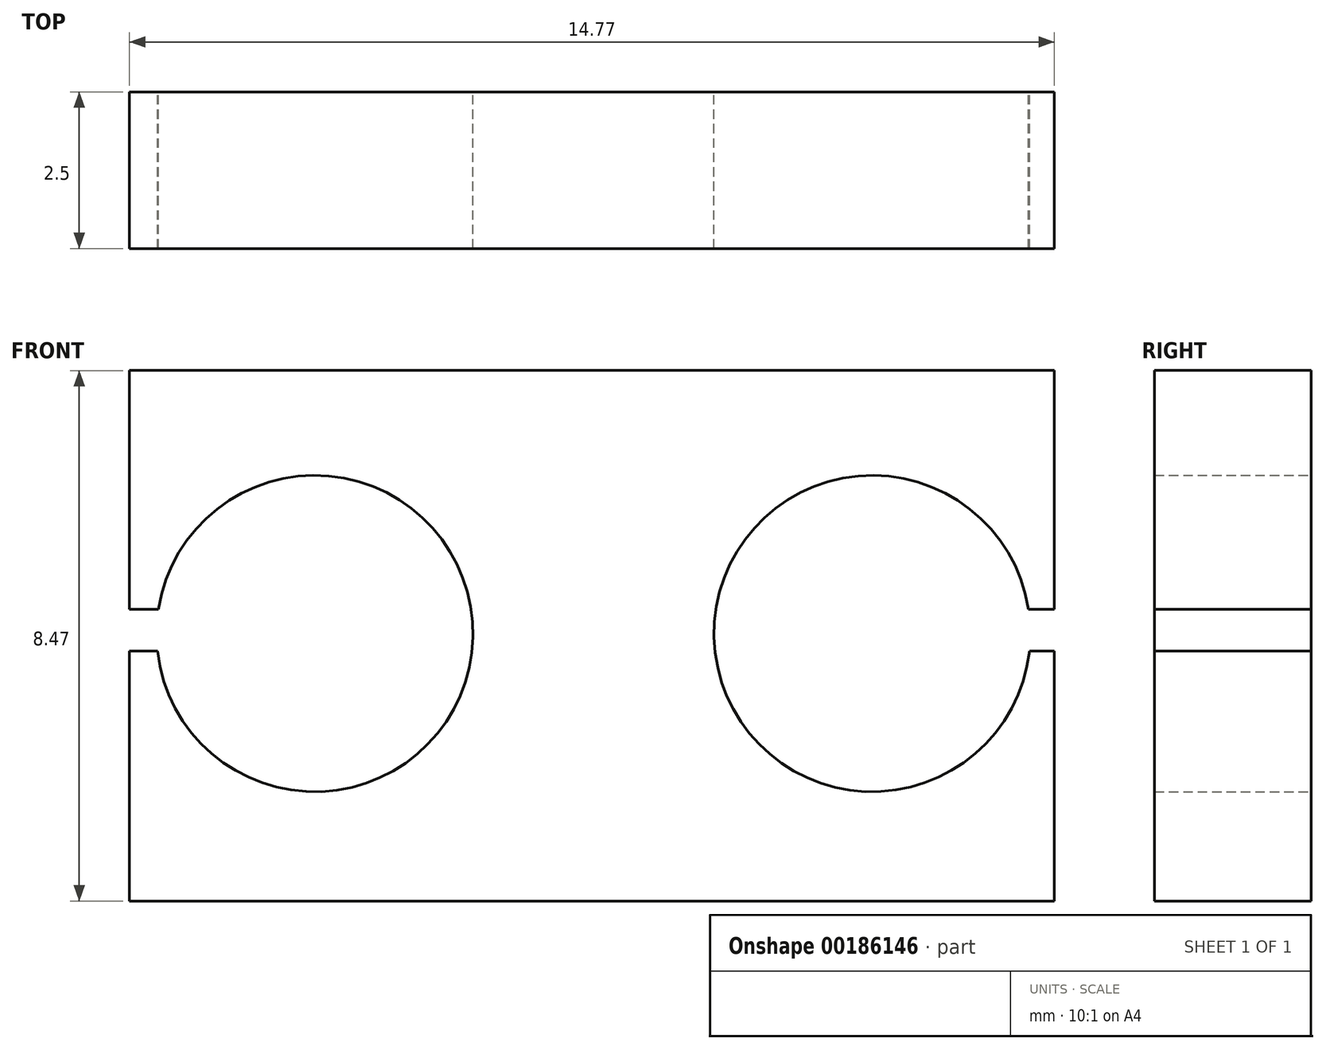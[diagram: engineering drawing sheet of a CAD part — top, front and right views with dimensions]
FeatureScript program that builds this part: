
annotation { "Feature Type Name" : "Feature", "Feature Type Description" : "" }
export const myFeature = defineFeature(function(context is Context, id is Id, definition is map)
    precondition{}
    {
        {
            var Q0;
            Q0=qCreatedBy(makeId("Front.planeOp"),FACE);
            var sketch = newSketch(context, id + "F0", { "sketchPlane" : qUnion([Q0])});
            skPoint(sketch, "E0.middle", {"position": v(0, 0) * mm});
            skArc(sketch, "E1", {"start": v(-6.96, -0.67) * mm, "mid": v(-1.93, -0.45) * mm, "end": v(-6.95, 0) * mm});
            skArc(sketch, "E2.MirrorCS", {"start": v(6.96, -0.67) * mm, "mid": v(1.93, -0.45) * mm, "end": v(6.95, 0) * mm});
            skLineSegment(sketch, "E3", {"start": v(-6.61, 3.81) * mm, "end": v(7.36, 3.81) * mm});
            skLineSegment(sketch, "E4", {"start": v(-6.81, -4.66) * mm, "end": v(7.36, -4.66) * mm});
            skLineSegment(sketch, "E5", {"start": v(-6.95, 0) * mm, "end": v(-6.95, 0) * mm});
            skLineSegment(sketch, "E6", {"start": v(6.95, 0) * mm, "end": v(7.36, 0) * mm});
            skLineSegment(sketch, "E7", {"start": v(7.36, 0) * mm, "end": v(7.36, 3.81) * mm});
            skLineSegment(sketch, "E8", {"start": v(6.96, -0.67) * mm, "end": v(7.36, -0.67) * mm});
            skLineSegment(sketch, "E9", {"start": v(7.36, -0.67) * mm, "end": v(7.36, -4.66) * mm});
            skLineSegment(sketch, "E10", {"start": v(-6.61, 3.81) * mm, "end": v(-7.41, 3.81) * mm});
            skLineSegment(sketch, "E11", {"start": v(-7.41, 3.81) * mm, "end": v(-7.41, 0) * mm});
            skLineSegment(sketch, "E12", {"start": v(-7.41, 0) * mm, "end": v(-6.95, 0) * mm});
            skLineSegment(sketch, "E13", {"start": v(-6.96, -0.67) * mm, "end": v(-7.41, -0.67) * mm});
            skLineSegment(sketch, "E14", {"start": v(-7.41, -0.67) * mm, "end": v(-7.41, -4.66) * mm});
            skLineSegment(sketch, "E15", {"start": v(-7.41, -4.66) * mm, "end": v(-6.81, -4.66) * mm});
            skPoint(sketch, "E16.end.orphan", {"position": v(-6.95, -0.67) * mm});
            skSolve(sketch);
        }
        {
            var Q0;
            {var subQ0=sQuery(id+"F0.wireOp",EDGE,"E1");Q0=makeQuery(id+"F0.imprint","IMPRINT",FACE,{"disambiguationData":[TD([[makeQuery(id+"F0.imprint","IMPRINT",EDGE,{"derivedFrom":subQ0}),-1.0]])]});}
            extrude(context, id + "F1", {"entities" : qUnion([Q0]), "depth" : 2.5 * mm});
        }
    });
